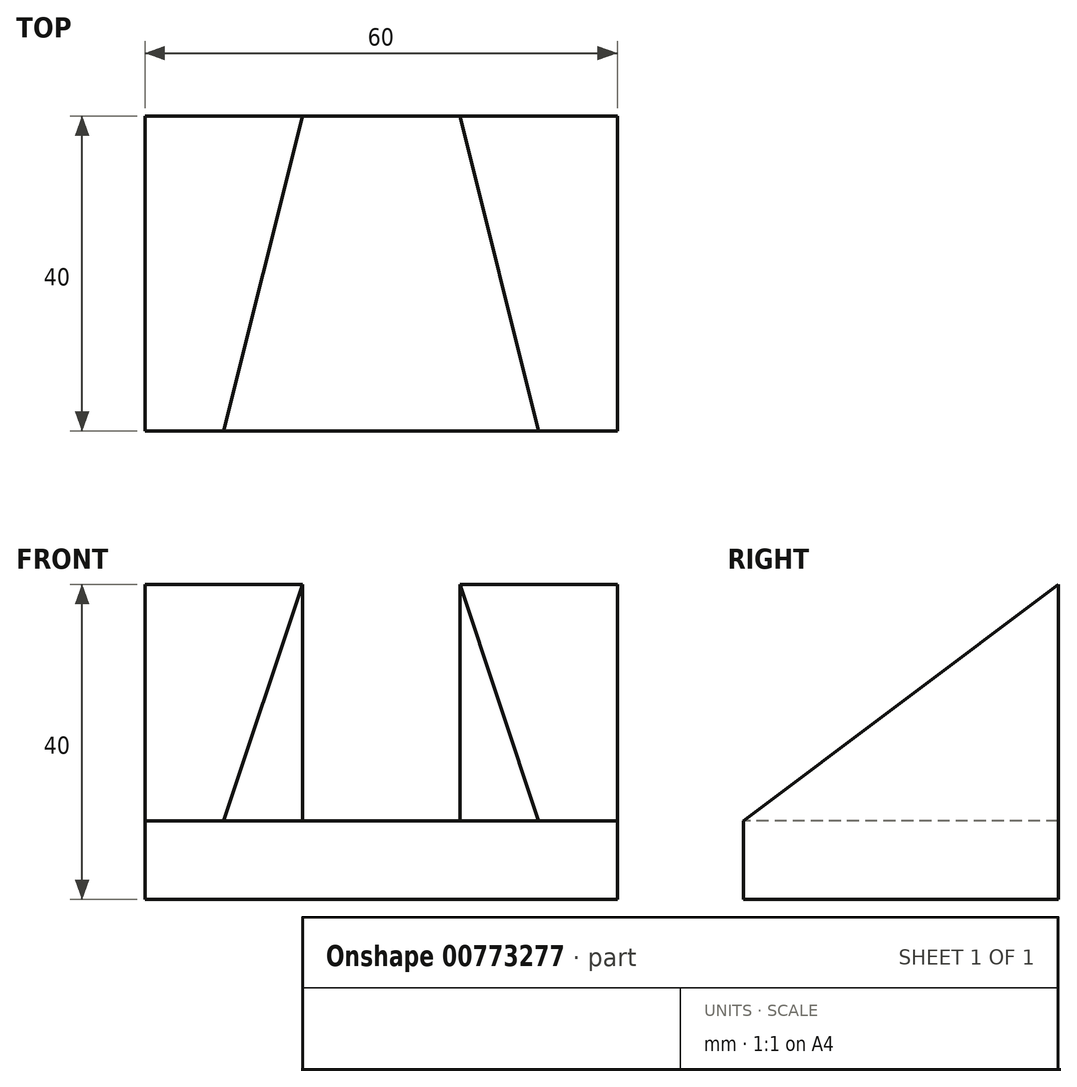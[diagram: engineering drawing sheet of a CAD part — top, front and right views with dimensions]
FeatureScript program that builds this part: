
annotation { "Feature Type Name" : "Feature", "Feature Type Description" : "" }
export const myFeature = defineFeature(function(context is Context, id is Id, definition is map)
    precondition{}
    {
        {
            var Q0;
            Q0=qCreatedBy(makeId("Top.planeOp"),FACE);
            var sketch = newSketch(context, id + "F0", { "sketchPlane" : qUnion([Q0])});
            skLineSegment(sketch, "E0.bottom", {"start": v(-27.48, 26.72) * mm, "end": v(32.52, 26.72) * mm});
            skLineSegment(sketch, "E0.top", {"start": v(-27.48, -13.28) * mm, "end": v(32.52, -13.28) * mm});
            skLineSegment(sketch, "E0.left", {"start": v(-27.48, 26.72) * mm, "end": v(-27.48, -13.28) * mm});
            skLineSegment(sketch, "E0.right", {"start": v(32.52, 26.72) * mm, "end": v(32.52, -13.28) * mm});
            skSolve(sketch);
        }
        {
            var Q0;
            Q0=makeQuery(id+"F0.imprint","IMPRINT",FACE,{"disambiguationData":[TD([[makeQuery(id+"F0.imprint","IMPRINT",EDGE,{"derivedFrom":sQuery(id+"F0.wireOp",EDGE,"E0.bottom")}),-1.0]])]});
            extrude(context, id + "F1", {"entities" : qUnion([Q0]), "depth" : 10 * mm, "offsetDistance" : 25.4 * mm});
        }
        {
            var Q0;
            Q0=makeQuery(id+"F1.opExtrude","CAP_FACE",FACE,{"disambiguationData":[OSD([sQuery(id+"F0.wireOp",EDGE,"E0.bottom"),sQuery(id+"F0.wireOp",EDGE,"E0.top"),sQuery(id+"F0.wireOp",EDGE,"E0.left"),sQuery(id+"F0.wireOp",EDGE,"E0.right")])],"isStart":false});
            var sketch = newSketch(context, id + "F2", { "sketchPlane" : qUnion([Q0])});
            skLineSegment(sketch, "E1", {"start": v(-27.48, 26.72) * mm, "end": v(-7.48, 26.72) * mm});
            skLineSegment(sketch, "E2", {"start": v(-7.48, 26.72) * mm, "end": v(-17.48, -13.28) * mm});
            skLineSegment(sketch, "E3", {"start": v(-17.48, -13.28) * mm, "end": v(-27.48, -13.28) * mm});
            skLineSegment(sketch, "E4", {"start": v(-27.48, 26.72) * mm, "end": v(-27.48, -13.28) * mm});
            skLineSegment(sketch, "E5", {"start": v(32.52, 26.72) * mm, "end": v(12.52, 26.72) * mm});
            skLineSegment(sketch, "E6", {"start": v(12.52, 26.72) * mm, "end": v(22.52, -13.28) * mm});
            skLineSegment(sketch, "E7", {"start": v(22.52, -13.28) * mm, "end": v(32.52, -13.28) * mm});
            skLineSegment(sketch, "E8", {"start": v(32.52, 26.72) * mm, "end": v(32.52, -13.28) * mm});
            skSolve(sketch);
        }
        {
            var Q0;
            Q0=makeQuery(id+"F2.imprint","IMPRINT",FACE,{"disambiguationData":[TD([[makeQuery(id+"F2.imprint","IMPRINT",EDGE,{"derivedFrom":sQuery(id+"F2.wireOp",EDGE,"E1")}),-1.0]])]});
            var Q1;
            Q1=makeQuery(id+"F2.imprint","IMPRINT",FACE,{"disambiguationData":[TD([[makeQuery(id+"F2.imprint","IMPRINT",EDGE,{"derivedFrom":sQuery(id+"F2.wireOp",EDGE,"E5")}),-1.0]])]});
            extrude(context, id + "F3", {"entities" : qUnion([Q0, Q1]), "operationType" : NewBodyOperationType.ADD, "depth" : 30 * mm, "offsetDistance" : 25.4 * mm});
        }
        {
            var Q0;
            Q0=makeQuery(id+"F3.boolean.opBoolean","MERGE",FACE,{"derivedFrom":[makeQuery(id+"F1.opExtrude","SWEPT_FACE",FACE,{"disambiguationData":[OSD([sQuery(id+"F0.wireOp",EDGE,"E0.left")])]}),makeQuery(id+"F3.opExtrude","SWEPT_FACE",FACE,{"disambiguationData":[OSD([sQuery(id+"F2.wireOp",EDGE,"E4")])]})]});
            var sketch = newSketch(context, id + "F4", { "sketchPlane" : qUnion([Q0])});
            skLineSegment(sketch, "E9", {"start": v(13.28, 0) * mm, "end": v(13.28, 10) * mm});
            skLineSegment(sketch, "E10", {"start": v(13.28, 10) * mm, "end": v(-26.72, 40) * mm});
            skLineSegment(sketch, "E11", {"start": v(-26.72, 40) * mm, "end": v(13.28, 40) * mm});
            skLineSegment(sketch, "E12", {"start": v(13.28, 40) * mm, "end": v(13.28, 10) * mm});
            skSolve(sketch);
        }
        {
            var Q0;
            Q0=makeQuery(id+"F4.imprint","IMPRINT",FACE,{"disambiguationData":[TD([[makeQuery(id+"F4.imprint","IMPRINT",EDGE,{"derivedFrom":sQuery(id+"F4.wireOp",EDGE,"E10")}),-1.0]])]});
            extrude(context, id + "F5", {"entities" : qUnion([Q0]), "operationType" : NewBodyOperationType.REMOVE, "oppositeDirection" : true, "depth" : 60 * mm, "offsetDistance" : 25.4 * mm});
        }
    });
